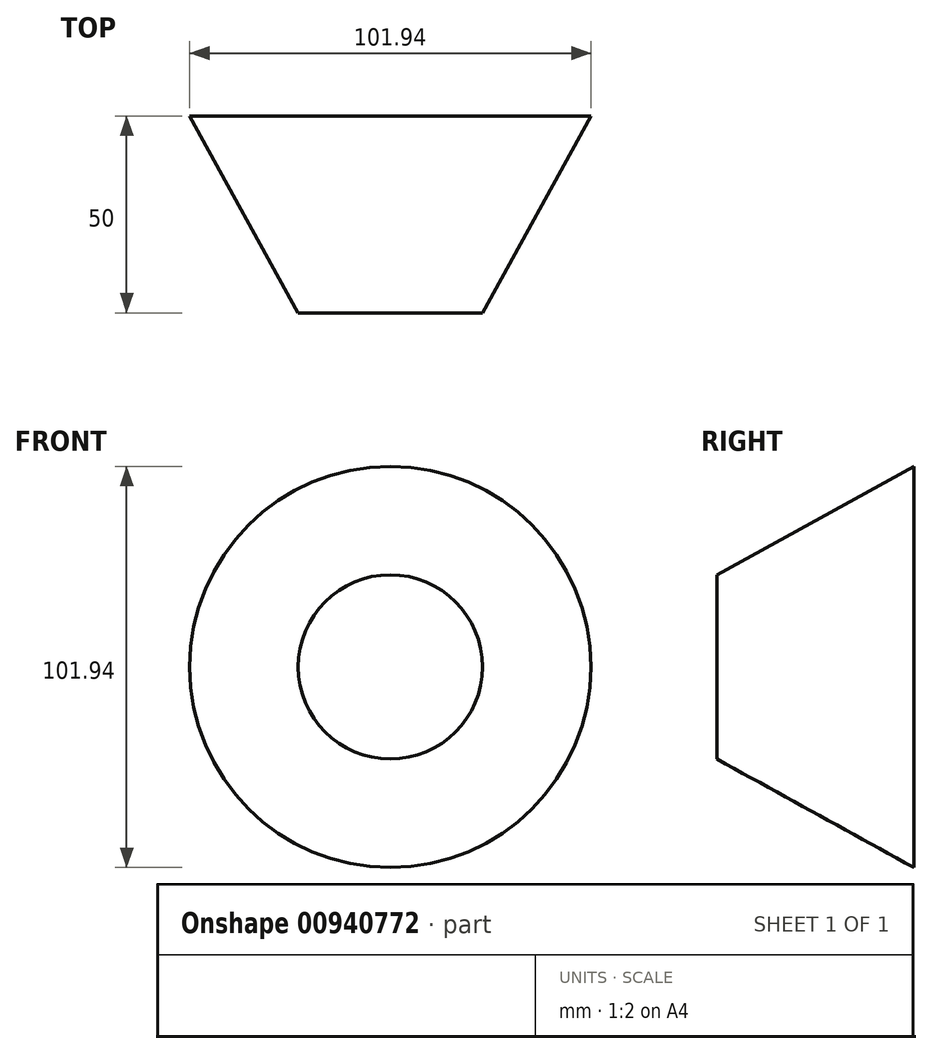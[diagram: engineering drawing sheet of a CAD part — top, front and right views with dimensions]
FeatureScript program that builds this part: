
annotation { "Feature Type Name" : "Feature", "Feature Type Description" : "" }
export const myFeature = defineFeature(function(context is Context, id is Id, definition is map)
    precondition{}
    {
        {
            var Q0;
            Q0=qCreatedBy(makeId("Front.planeOp"),FACE);
            cPlane(context, id + "F0", {"entities" : qUnion([Q0]), "cplaneType" : CPlaneType.OFFSET, "offset" : 25 * mm, "width" : 150 * mm, "height" : 150 * mm});
        }
        {
            var Q0;
            Q0=qCreatedBy(makeId("Front.planeOp"),FACE);
            cPlane(context, id + "F1", {"entities" : qUnion([Q0]), "cplaneType" : CPlaneType.OFFSET, "offset" : 25 * mm, "oppositeDirection" : true, "width" : 150 * mm, "height" : 150 * mm});
        }
        {
            var Q0;
            Q0=qCreatedBy(id+"F1.planeOp",FACE);
            var sketch = newSketch(context, id + "F2", { "sketchPlane" : qUnion([Q0])});
            skCircle(sketch, "E0", {"center": v(0, 0) * mm, "radius": 65.96 * mm});
            skCircle(sketch, "E1", {"center": v(0, 0) * mm, "radius": 50.97 * mm});
            skSolve(sketch);
        }
        {
            var Q0;
            Q0=qCreatedBy(id+"F0.planeOp",FACE);
            var sketch = newSketch(context, id + "F3", { "sketchPlane" : qUnion([Q0])});
            skCircle(sketch, "E2", {"center": v(0, 0) * mm, "radius": 31.2 * mm});
            skCircle(sketch, "E3", {"center": v(0, 0) * mm, "radius": 23.4 * mm});
            skSolve(sketch);
        }
        {
            var Q0;
            Q0=makeQuery(id+"F2.imprint","IMPRINT",FACE,{"disambiguationData":[TD([[makeQuery(id+"F2.imprint","IMPRINT",EDGE,{"derivedFrom":sQuery(id+"F2.wireOp",EDGE,"E1")}),1.0]])]});
            var Q1;
            Q1=makeQuery(id+"F3.imprint","IMPRINT",FACE,{"disambiguationData":[TD([[makeQuery(id+"F3.imprint","IMPRINT",EDGE,{"derivedFrom":sQuery(id+"F3.wireOp",EDGE,"E3")}),1.0]])]});
            loft(context, id + "F4", {"sheetProfilesArray" : [{ "sheetProfileEntities" : qUnion([Q0]) }, { "sheetProfileEntities" : qUnion([Q1]) }]});
        }
    });
